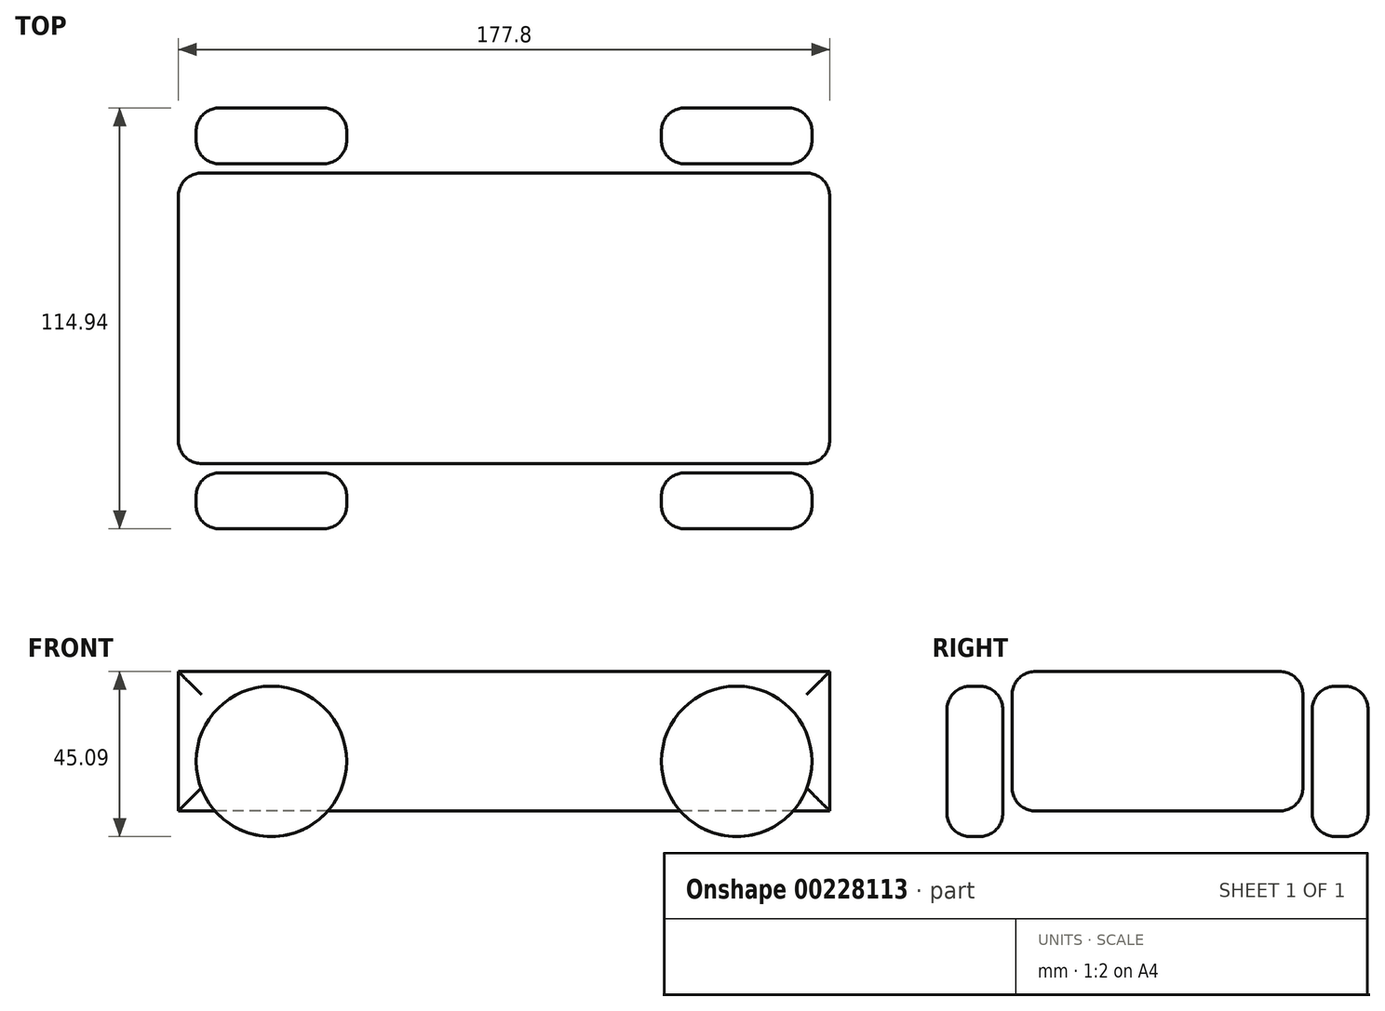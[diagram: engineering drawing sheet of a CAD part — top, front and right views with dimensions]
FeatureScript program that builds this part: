
annotation { "Feature Type Name" : "Feature", "Feature Type Description" : "" }
export const myFeature = defineFeature(function(context is Context, id is Id, definition is map)
    precondition{}
    {
        {
            var Q0;
            Q0=qCreatedBy(makeId("Front.planeOp"),FACE);
            var sketch = newSketch(context, id + "F0", { "sketchPlane" : qUnion([Q0])});
            skLineSegment(sketch, "E0.bottom", {"start": v(88.9, 19.05) * mm, "end": v(-88.9, 19.05) * mm});
            skLineSegment(sketch, "E0.top", {"start": v(88.9, -19.05) * mm, "end": v(-88.9, -19.05) * mm});
            skLineSegment(sketch, "E0.left", {"start": v(88.9, 19.05) * mm, "end": v(88.9, -19.05) * mm});
            skLineSegment(sketch, "E0.right", {"start": v(-88.9, 19.05) * mm, "end": v(-88.9, -19.05) * mm});
            skPoint(sketch, "E0.middle", {"position": v(0, 0) * mm});
            skLineSegment(sketch, "E1", {"start": v(-100.11, -26.04) * mm, "end": v(104.43, -26.03) * mm, "construction": true});
            skCircle(sketch, "E2", {"center": v(63.5, -5.5) * mm, "radius": 20.54 * mm});
            skSolve(sketch);
        }
        {
            var Q0;
            Q0=qCreatedBy(makeId("Front.planeOp"),FACE);
            var sketch = newSketch(context, id + "F1", { "sketchPlane" : qUnion([Q0])});
            skLineSegment(sketch, "E3.0", {"start": v(88.9, 19.05) * mm, "end": v(-88.9, 19.05) * mm});
            skLineSegment(sketch, "E4.0", {"start": v(-88.9, 19.05) * mm, "end": v(-88.9, -19.05) * mm});
            skLineSegment(sketch, "E5.0", {"start": v(88.9, -19.05) * mm, "end": v(-88.9, -19.05) * mm});
            skLineSegment(sketch, "E6.0", {"start": v(88.9, 19.05) * mm, "end": v(88.9, -19.05) * mm});
            skSolve(sketch);
        }
        {
            var Q0;
            Q0 = qSketchRegion(id + "F1", true);
            extrude(context, id + "F2", {"entities" : qUnion([Q0]), "endBound" : BoundingType.SYMMETRIC, "depth" : 79.38 * mm});
        }
        {
            var Q0;
            Q0=makeQuery(id+"F2.opExtrude","CAP_FACE",FACE,{"disambiguationData":[OSD([sQuery(id+"F1.wireOp",EDGE,"E3.0"),sQuery(id+"F1.wireOp",EDGE,"E4.0"),sQuery(id+"F1.wireOp",EDGE,"E5.0"),sQuery(id+"F1.wireOp",EDGE,"E6.0")])],"isStart":false});
            cPlane(context, id + "F3", {"entities" : qUnion([Q0]), "cplaneType" : CPlaneType.OFFSET, "offset" : 2.54 * mm, "width" : 152.4 * mm, "height" : 152.4 * mm});
        }
        {
            var Q0;
            Q0=qCreatedBy(id+"F3.planeOp",FACE);
            var sketch = newSketch(context, id + "F4", { "sketchPlane" : qUnion([Q0])});
            skCircle(sketch, "E7.0", {"center": v(63.5, -5.5) * mm, "radius": 20.54 * mm});
            skSolve(sketch);
        }
        {
            var Q0;
            Q0 = qSketchRegion(id + "F4", true);
            extrude(context, id + "F5", {"entities" : qUnion([Q0]), "depth" : 15.24 * mm});
        }
        {
            var Q0;
            Q0=makeQuery(id+"F5.opExtrude","SWEPT_FACE",FACE,{"disambiguationData":[OSD([sQuery(id+"F4.wireOp",EDGE,"E7.0")])]});
            fillet(context, id + "F6", {"entities" : qUnion([Q0]), "radius" : 6.35 * mm, "tangentPropagation" : true, "allowEdgeOverflow" : false});
        }
        {
            var Q0;
            Q0=makeQuery(id+"F5.opExtrude","SWEPT_BODY",BODY,{"disambiguationData":[OSD([sQuery(id+"F4.wireOp",EDGE,"E7.0")])]});
            var Q1;
            Q1=qCreatedBy(makeId("Front.planeOp"),FACE);
            mirror(context, id + "F7", {"entities" : qUnion([Q0]), "mirrorPlane" : qUnion([Q1])});
        }
        {
            var Q0;
            Q0=makeQuery(id+"F2.opExtrude","CAP_FACE",FACE,{"disambiguationData":[OSD([sQuery(id+"F1.wireOp",EDGE,"E3.0"),sQuery(id+"F1.wireOp",EDGE,"E4.0"),sQuery(id+"F1.wireOp",EDGE,"E5.0"),sQuery(id+"F1.wireOp",EDGE,"E6.0")])],"isStart":false});
            var Q1;
            Q1=makeQuery(id+"F2.opExtrude","CAP_FACE",FACE,{"disambiguationData":[OSD([sQuery(id+"F1.wireOp",EDGE,"E3.0"),sQuery(id+"F1.wireOp",EDGE,"E4.0"),sQuery(id+"F1.wireOp",EDGE,"E5.0"),sQuery(id+"F1.wireOp",EDGE,"E6.0")])],"isStart":true});
            fillet(context, id + "F8", {"entities" : qUnion([Q0, Q1]), "radius" : 6.35 * mm, "tangentPropagation" : true, "allowEdgeOverflow" : false});
        }
        {
            var Q0;
            Q0=makeQuery(id+"F5.opExtrude","SWEPT_BODY",BODY,{"disambiguationData":[OSD([sQuery(id+"F4.wireOp",EDGE,"E7.0")])]});
            var Q1;
            Q1=makeQuery(id+"F7.opPattern","COPY",BODY,{"derivedFrom":makeQuery(id+"F5.opExtrude","SWEPT_BODY",BODY,{"disambiguationData":[OSD([sQuery(id+"F4.wireOp",EDGE,"E7.0")])]}),"instanceName":"1"});
            var Q2;
            Q2=qCreatedBy(makeId("Right.planeOp"),FACE);
            mirror(context, id + "F9", {"entities" : qUnion([Q0, Q1]), "mirrorPlane" : qUnion([Q2])});
        }
    });
